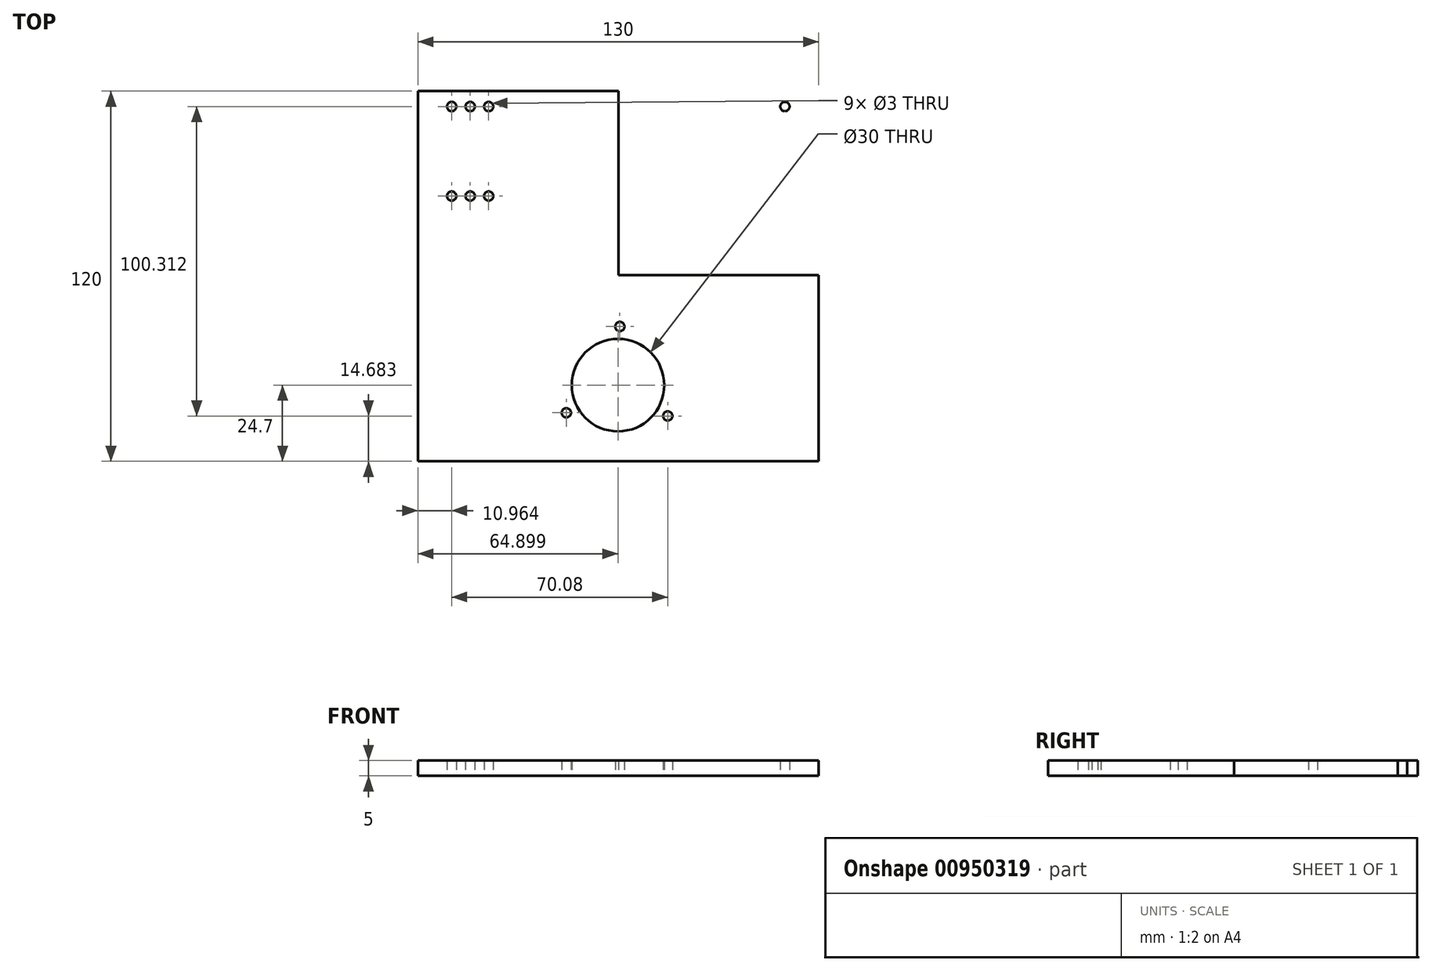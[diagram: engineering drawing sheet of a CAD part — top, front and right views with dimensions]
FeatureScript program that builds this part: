
annotation { "Feature Type Name" : "Feature", "Feature Type Description" : "" }
export const myFeature = defineFeature(function(context is Context, id is Id, definition is map)
    precondition{}
    {
        {
            var Q0;
            Q0=qCreatedBy(makeId("Top.planeOp"),FACE);
            var sketch = newSketch(context, id + "F0", { "sketchPlane" : qUnion([Q0])});
            skPoint(sketch, "E0.orphan", {"position": v(-1.01, 103.53) * mm});
            skLineSegment(sketch, "E1.bottom", {"start": v(-59.1, 59.65) * mm, "end": v(70.9, 59.65) * mm});
            skLineSegment(sketch, "E1.top", {"start": v(-59.1, -60.35) * mm, "end": v(70.9, -60.35) * mm});
            skLineSegment(sketch, "E1.left", {"start": v(-59.1, 59.65) * mm, "end": v(-59.1, -60.35) * mm});
            skLineSegment(sketch, "E1.right", {"start": v(70.9, 59.65) * mm, "end": v(70.9, -60.35) * mm});
            skLineSegment(sketch, "E2", {"start": v(5.9, 59.65) * mm, "end": v(5.9, -60.35) * mm});
            skLineSegment(sketch, "E3", {"start": v(70.9, 0) * mm, "end": v(-59.1, 0) * mm});
            skPoint(sketch, "E3.startSnap0", {"position": v(70.9, -0.35) * mm});
            skCircle(sketch, "E4", {"center": v(5.79, -35.65) * mm, "radius": 15 * mm});
            skLineSegment(sketch, "E5", {"start": v(5.79, -35.65) * mm, "end": v(5.9, -35.65) * mm});
            skCircle(sketch, "E6", {"center": v(6.4, -16.66) * mm, "radius": 1.5 * mm});
            skCircle(sketch, "E7.1.0", {"center": v(-10.96, -44.62) * mm, "radius": 1.5 * mm});
            skCircle(sketch, "E7.2.0", {"center": v(21.93, -45.67) * mm, "radius": 1.5 * mm});
            skCircle(sketch, "E8", {"center": v(-48.15, 25.64) * mm, "radius": 1.5 * mm});
            skCircle(sketch, "E9.0.1.0", {"center": v(-48.15, 54.64) * mm, "radius": 1.5 * mm});
            skCircle(sketch, "E9.1.0.0", {"center": v(-42.15, 25.64) * mm, "radius": 1.5 * mm});
            skCircle(sketch, "E9.1.1.0", {"center": v(-42.15, 54.64) * mm, "radius": 1.5 * mm});
            skCircle(sketch, "E9.2.0.0", {"center": v(-36.15, 25.64) * mm, "radius": 1.5 * mm});
            skCircle(sketch, "E9.2.1.0", {"center": v(-36.15, 54.64) * mm, "radius": 1.5 * mm});
            skLineSegment(sketch, "E9.direction1", {"start": v(-48.15, 25.64) * mm, "end": v(-42.15, 25.64) * mm, "construction": true});
            skLineSegment(sketch, "E9.direction2", {"start": v(-48.15, 25.64) * mm, "end": v(-48.15, 54.64) * mm, "construction": true});
            skCircle(sketch, "E10.MirrorC", {"center": v(59.93, 54.64) * mm, "radius": 1.5 * mm});
            skCircle(sketch, "E11.MirrorC", {"center": v(59.93, 25.64) * mm, "radius": 1.5 * mm});
            skCircle(sketch, "E12.MirrorC", {"center": v(53.93, 25.64) * mm, "radius": 1.5 * mm});
            skLineSegment(sketch, "E13.MirrorCS", {"start": v(59.93, 25.64) * mm, "end": v(59.93, 54.64) * mm, "construction": true});
            skLineSegment(sketch, "E14.MirrorCS", {"start": v(59.93, 25.64) * mm, "end": v(53.93, 25.64) * mm, "construction": true});
            skCircle(sketch, "E15.MirrorC", {"center": v(47.93, 25.64) * mm, "radius": 1.5 * mm});
            skCircle(sketch, "E16.MirrorC", {"center": v(47.93, 54.64) * mm, "radius": 1.5 * mm});
            skCircle(sketch, "E17.MirrorC", {"center": v(53.93, 54.64) * mm, "radius": 1.5 * mm});
            skSolve(sketch);
        }
        {
            var Q0;
            Q0=makeQuery(id+"F0.imprint","IMPRINT",FACE,{"disambiguationData":[TD([[makeQuery(id+"F0.imprint","IMPRINT",EDGE,{"derivedFrom":sQuery(id+"F0.wireOp",EDGE,"E7.1.0")}),-1.0]])]});
            var Q1;
            Q1=makeQuery(id+"F0.imprint","IMPRINT",FACE,{"disambiguationData":[TD([[makeQuery(id+"F0.imprint","IMPRINT",EDGE,{"derivedFrom":sQuery(id+"F0.wireOp",EDGE,"E8")}),-1.0]])]});
            var Q2;
            Q2=makeQuery(id+"F0.imprint","IMPRINT",FACE,{"disambiguationData":[TD([[makeQuery(id+"F0.imprint","IMPRINT",EDGE,{"derivedFrom":sQuery(id+"F0.wireOp",EDGE,"E10.MirrorC")}),1.0]])]});
            var Q3;
            Q3=makeQuery(id+"F0.imprint","IMPRINT",FACE,{"disambiguationData":[TD([[makeQuery(id+"F0.imprint","IMPRINT",EDGE,{"derivedFrom":sQuery(id+"F0.wireOp",EDGE,"E7.2.0")}),-1.0]])]});
            extrude(context, id + "F1", {"entities" : qUnion([Q0, Q1, Q2, Q3]), "depth" : 5 * mm, "offsetDistance" : 25 * mm});
        }
    });
